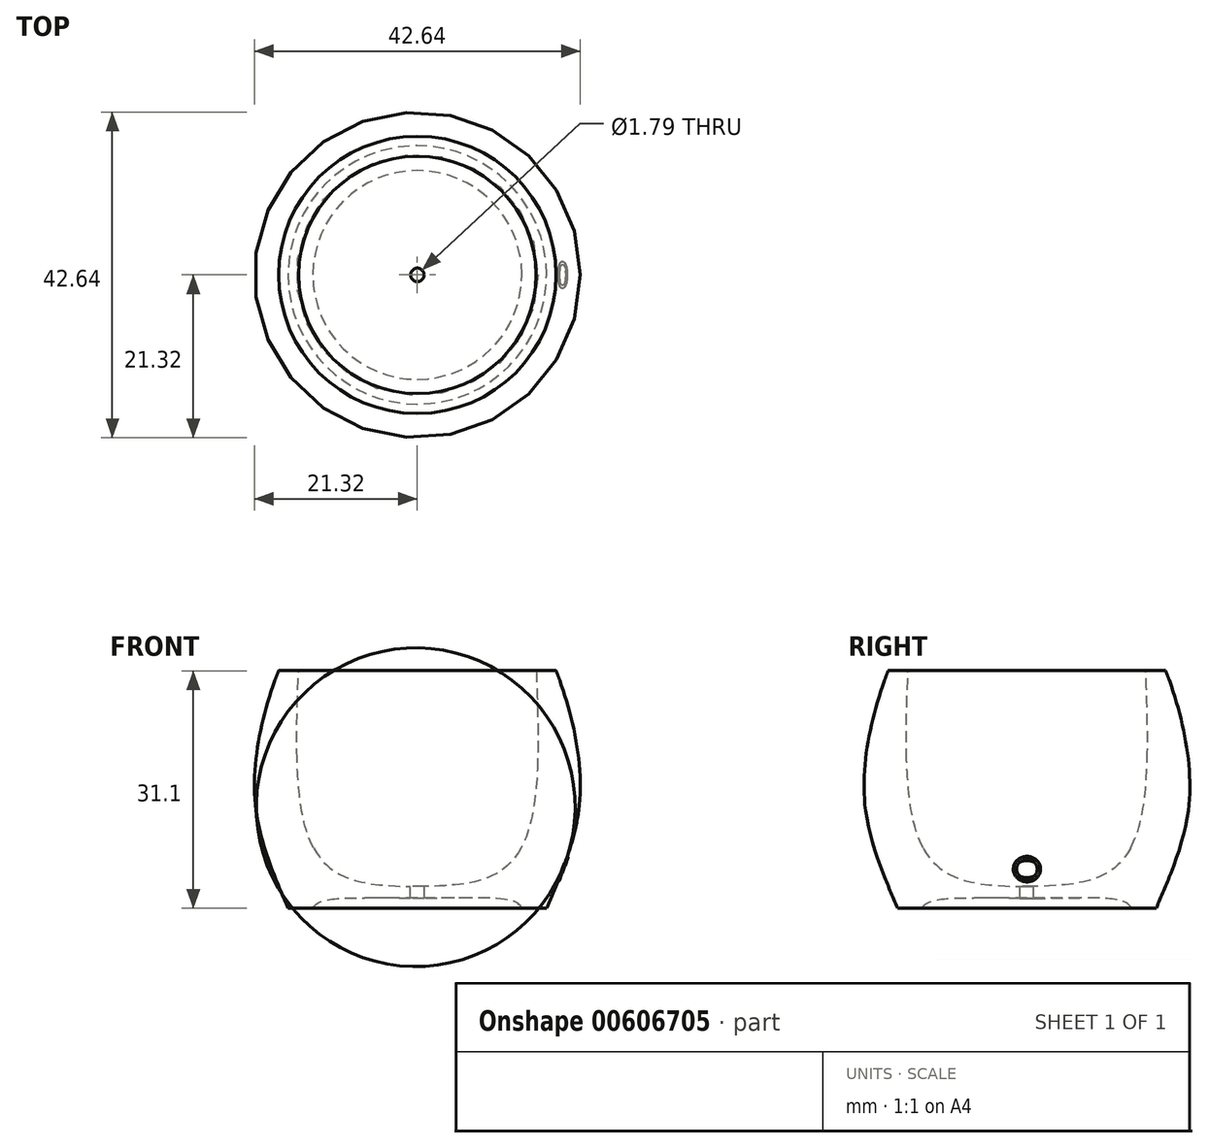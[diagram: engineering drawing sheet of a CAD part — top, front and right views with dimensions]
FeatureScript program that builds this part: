
annotation { "Feature Type Name" : "Feature", "Feature Type Description" : "" }
export const myFeature = defineFeature(function(context is Context, id is Id, definition is map)
    precondition{}
    {
        {
            var Q0;
            Q0=qCreatedBy(makeId("Front.planeOp"),FACE);
            var sketch = newSketch(context, id + "F0", { "sketchPlane" : qUnion([Q0])});
            skFitSpline(sketch, "E0", {"points": [v(18.15, 31.1) * mm, v(21.29, 14.83) * mm, v(16.9, 0) * mm], "startDerivative": vector(10.14, -25.77) * mm, "endDerivative": vector(-12.29, -28.95) * mm});
            skLineSegment(sketch, "E1", {"start": v(18.15, 31.1) * mm, "end": v(15.55, 31.1) * mm});
            skLineSegment(sketch, "E2", {"start": v(16.9, 0) * mm, "end": v(13.67, 0) * mm});
            skFitSpline(sketch, "E3", {"points": [v(13.67, 0) * mm, v(12.77, 0.85) * mm, v(0.9, 1.26) * mm], "startDerivative": vector(-2.23, 3.83) * mm, "endDerivative": vector(-20.25, -0.55) * mm});
            skLineSegment(sketch, "E4", {"start": v(0.9, 1.26) * mm, "end": v(0.9, 2.86) * mm});
            skFitSpline(sketch, "E5", {"points": [v(15.55, 31.1) * mm, v(14.78, 11.13) * mm, v(9.92, 4.32) * mm, v(0.9, 2.86) * mm], "startDerivative": vector(1.7, -43.82) * mm, "endDerivative": vector(-32.37, -0.72) * mm});
            skFitSpline(sketch, "E6", {"points": [v(21.1, 12.8) * mm, v(18.55, 10.12) * mm, v(13.55, 7.88) * mm], "startDerivative": vector(-3.43, -6.8) * mm, "endDerivative": vector(-10.32, -3.27) * mm});
            skFitSpline(sketch, "E7", {"points": [v(18.63, 29.84) * mm, v(16.98, 23.29) * mm, v(15.74, 19.41) * mm], "startDerivative": vector(-3.68, -3.44) * mm, "endDerivative": vector(-1.96, -7.53) * mm});
            skLineSegment(sketch, "E8", {"start": v(0, 26.2) * mm, "end": v(0, 15.05) * mm, "construction": true});
            skSolve(sketch);
        }
        {
            var Q0;
            {var subQ0=sQuery(id+"F0.wireOp",EDGE,"E1");Q0=makeQuery(id+"F0.imprint","IMPRINT",FACE,{"disambiguationData":[TD([[makeQuery(id+"F0.imprint","IMPRINT",EDGE,{"derivedFrom":subQ0}),1.0]])]});}
            var Q1;
            {var subQ0=sQuery(id+"F0.wireOp",EDGE,"E6");Q1=makeQuery(id+"F0.imprint","IMPRINT",FACE,{"disambiguationData":[TD([[makeQuery(id+"F0.imprint","IMPRINT",EDGE,{"derivedFrom":subQ0}),-1.0]])]});}
            var Q2;
            {var subQ1=sQuery(id+"F0.wireOp",EDGE,"E2");Q2=makeQuery(id+"F0.imprint","IMPRINT",FACE,{"disambiguationData":[TD([[makeQuery(id+"F0.imprint","IMPRINT",EDGE,{"derivedFrom":subQ1}),-1.0]])]});}
            var Q3;
            Q3=sQuery(id+"F0.wireOp",EDGE,"E8");
            var Q4;
            Q4=sQuery(id+"F0.wireOp",EDGE,"E8");
            revolve(context, id + "F1", {"entities" : qUnion([Q0, Q1, Q2]), "surfaceEntities" : qUnion([Q3]), "axis" : qUnion([Q4]), "revolveType" : RevolveType.FULL});
        }
        {
            var Q0;
            Q0=qCreatedBy(makeId("Front.planeOp"),FACE);
            var sketch = newSketch(context, id + "F2", { "sketchPlane" : qUnion([Q0])});
            skLineSegment(sketch, "E9", {"start": v(18.36, 3.47) * mm, "end": v(19.56, 6.63) * mm});
            skLineSegment(sketch, "E10", {"start": v(20.76, 4.46) * mm, "end": v(17.22, 5.8) * mm});
            skFitSpline(sketch, "E11", {"points": [v(18.36, 3.47) * mm, v(17.95, 3.84) * mm, v(17.95, 5.53) * mm], "startDerivative": vector(-1.33, 0.72) * mm, "endDerivative": vector(0.34, 3.18) * mm});
            skFitSpline(sketch, "E12", {"points": [v(18.15, 5.46) * mm, v(18.1, 4.85) * mm, v(18.51, 3.87) * mm], "startDerivative": vector(-0.31, -1.34) * mm, "endDerivative": vector(0.98, -1.82) * mm});
            skFitSpline(sketch, "E13", {"points": [v(18.36, 3.47) * mm, v(18.56, 3.6) * mm, v(18.51, 3.87) * mm], "startDerivative": vector(0.52, 0.2) * mm, "endDerivative": vector(-0.21, 0.59) * mm});
            skFitSpline(sketch, "E14", {"points": [v(18.51, 3.87) * mm, v(18.79, 4.41) * mm, v(19.08, 5.1) * mm], "startDerivative": vector(0.58, 1.11) * mm, "endDerivative": vector(0.56, 1.35) * mm});
            skSolve(sketch);
        }
        {
            var Q0;
            Q0 = qSketchRegion(id + "F2", true);
            var Q1;
            Q1=sQuery(id+"F2.wireOp",EDGE,"E10");
            revolve(context, id + "F3", {"operationType" : NewBodyOperationType.ADD, "entities" : qUnion([Q0]), "axis" : qUnion([Q1]), "revolveType" : RevolveType.FULL});
        }
    });
